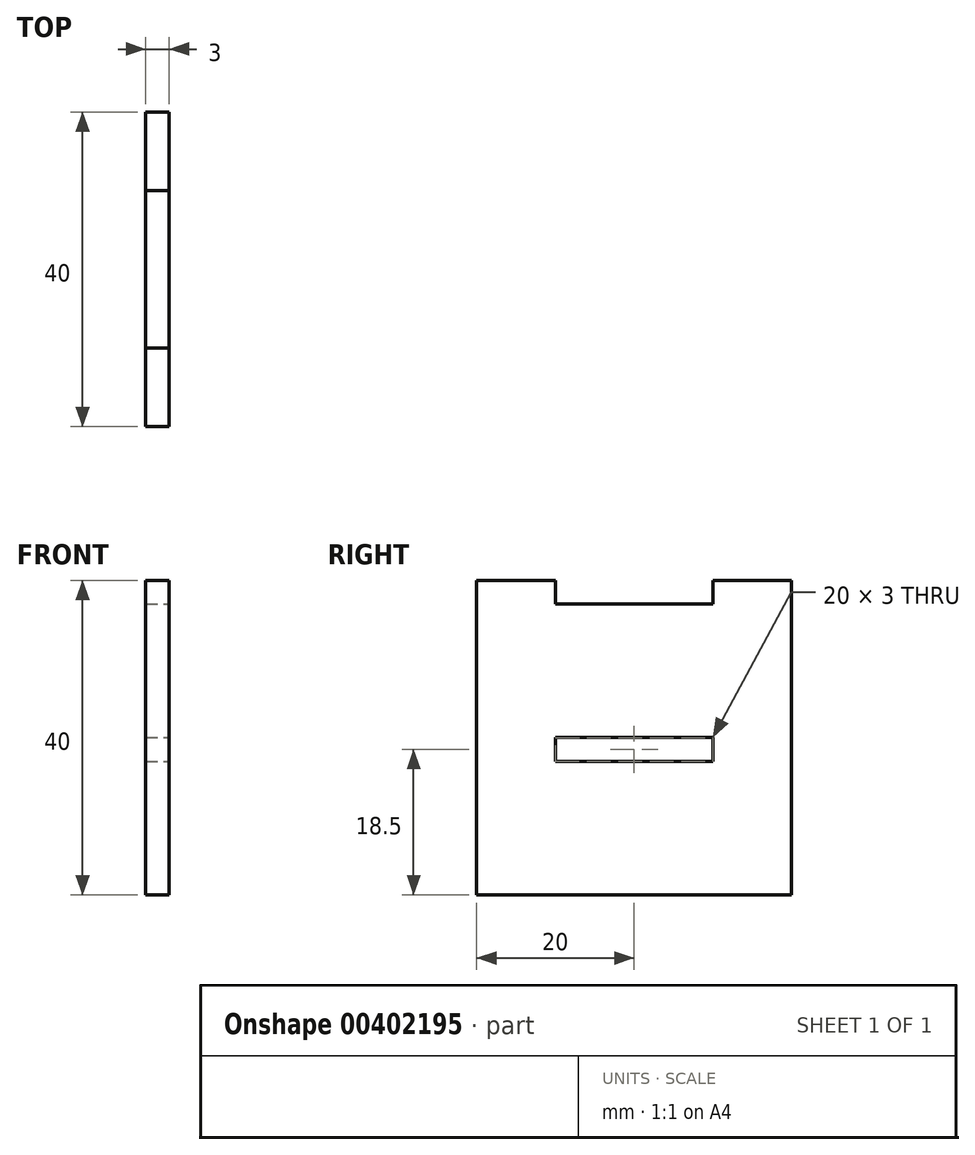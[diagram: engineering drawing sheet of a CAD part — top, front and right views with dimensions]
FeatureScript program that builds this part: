
annotation { "Feature Type Name" : "Feature", "Feature Type Description" : "" }
export const myFeature = defineFeature(function(context is Context, id is Id, definition is map)
    precondition{}
    {
        {
            assignVariable(context, id + "F0", {"name" : "t", "anyValue" : 3});
        }
        {
            var Q0;
            Q0=qCreatedBy(makeId("Right.planeOp"),FACE);
            var sketch = newSketch(context, id + "F1", { "sketchPlane" : qUnion([Q0])});
            skLineSegment(sketch, "E0.bottom", {"start": v(20, -20) * mm, "end": v(-20, -20) * mm});
            skLineSegment(sketch, "E0.top", {"start": v(20, 20) * mm, "end": v(-20, 20) * mm});
            skLineSegment(sketch, "E0.left", {"start": v(20, -20) * mm, "end": v(20, 20) * mm});
            skLineSegment(sketch, "E0.right", {"start": v(-20, -20) * mm, "end": v(-20, 20) * mm});
            skPoint(sketch, "E0.middle", {"position": v(0, 0) * mm});
            skLineSegment(sketch, "E1.bottom", {"start": v(-10, 20) * mm, "end": v(10, 20) * mm});
            skLineSegment(sketch, "E1.top", {"start": v(-10, 17) * mm, "end": v(10, 17) * mm});
            skLineSegment(sketch, "E1.left", {"start": v(-10, 20) * mm, "end": v(-10, 17) * mm});
            skLineSegment(sketch, "E1.right", {"start": v(10, 20) * mm, "end": v(10, 17) * mm});
            skLineSegment(sketch, "E2.0.1.0", {"start": v(-10, 0) * mm, "end": v(10, 0) * mm});
            skLineSegment(sketch, "E2.0.1.1", {"start": v(-10, -3) * mm, "end": v(10, -3) * mm});
            skLineSegment(sketch, "E2.0.1.2", {"start": v(-10, 0) * mm, "end": v(-10, -3) * mm});
            skLineSegment(sketch, "E2.0.1.3", {"start": v(10, 0) * mm, "end": v(10, -3) * mm});
            skLineSegment(sketch, "E2.direction1", {"start": v(-10, 17) * mm, "end": v(15, 17) * mm, "construction": true});
            skLineSegment(sketch, "E2.direction2", {"start": v(-10, 17) * mm, "end": v(-10, -3) * mm, "construction": true});
            skSolve(sketch);
        }
        {
            var Q0;
            Q0=makeQuery(id+"F1.imprint","IMPRINT",FACE,{"disambiguationData":[TD([[makeQuery(id+"F1.imprint","IMPRINT",EDGE,{"derivedFrom":sQuery(id+"F1.wireOp",EDGE,"E0.bottom")}),-1.0]])]});
            extrude(context, id + "F2", {"entities" : qUnion([Q0]), "oppositeDirection" : true, "depth" : getVariable(context, 't') * mm});
        }
    });
